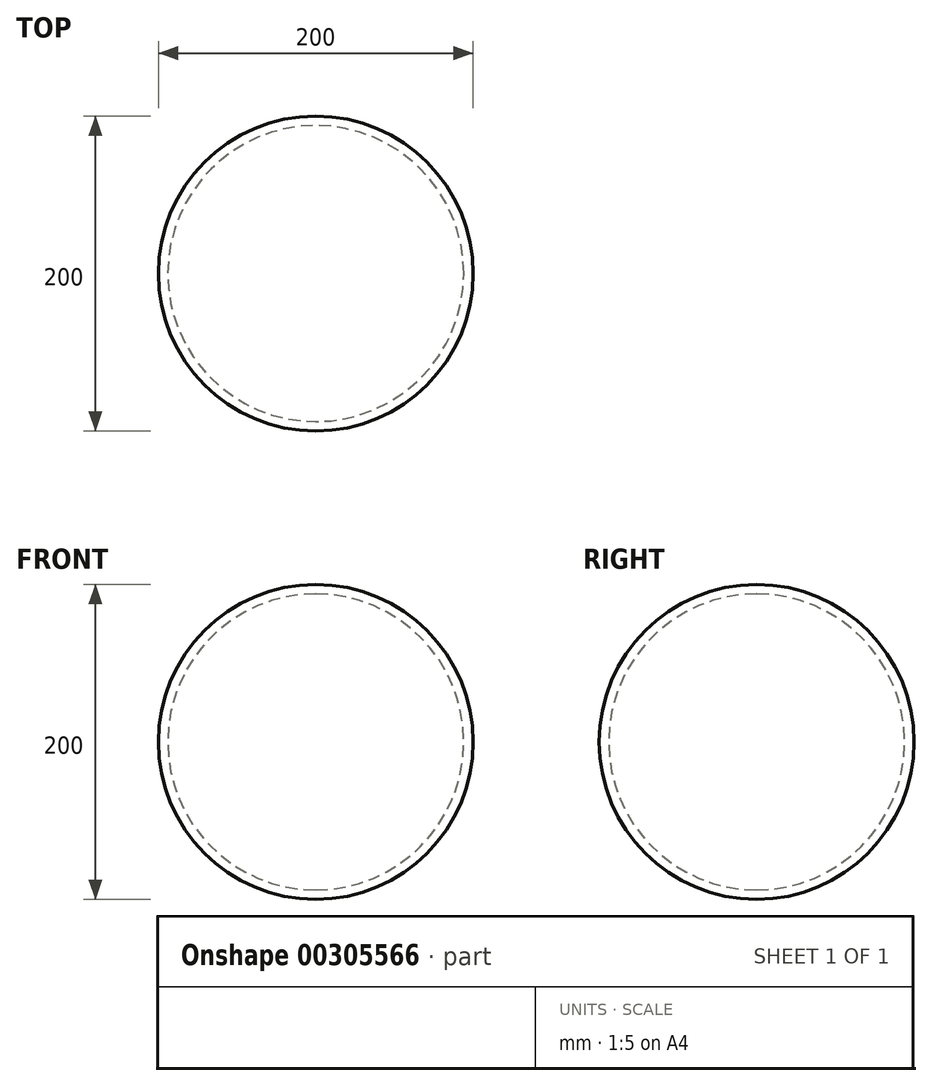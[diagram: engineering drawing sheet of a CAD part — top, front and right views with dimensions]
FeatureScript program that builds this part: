
annotation { "Feature Type Name" : "Feature", "Feature Type Description" : "" }
export const myFeature = defineFeature(function(context is Context, id is Id, definition is map)
    precondition{}
    {
        {
            var Q0;
            Q0=qCreatedBy(makeId("Front.planeOp"),FACE);
            var sketch = newSketch(context, id + "F0", { "sketchPlane" : qUnion([Q0])});
            skArc(sketch, "E0", {"start": v(0, 100) * mm, "mid": v(100, 0) * mm, "end": v(0, -100) * mm});
            skLineSegment(sketch, "E1", {"start": v(0, 100) * mm, "end": v(0, -100) * mm});
            skSolve(sketch);
        }
        {
            var Q0;
            Q0 = qSketchRegion(id + "F0", true);
            var Q1;
            Q1=sQuery(id+"F0.wireOp",EDGE,"E1");
            revolve(context, id + "F1", {"entities" : qUnion([Q0]), "axis" : qUnion([Q1]), "revolveType" : RevolveType.FULL});
        }
        {
            var Q0;
            Q0=makeQuery(id+"F1.opRevolve","SWEPT_FACE",FACE,{"disambiguationData":[OSD([sQuery(id+"F0.wireOp",EDGE,"E0")])]});
            var Q1;
            Q1=makeQuery(id+"F1.opRevolve","SWEPT_BODY",BODY,{"disambiguationData":[OSD([sQuery(id+"F0.wireOp",EDGE,"E0"),sQuery(id+"F0.wireOp",EDGE,"E1")])]});
            shell(context, id + "F2", {"isHollow" : true, "entities" : qUnion([Q0]), "parts" : qUnion([Q1]), "thickness" : 6 * mm});
        }
    });
